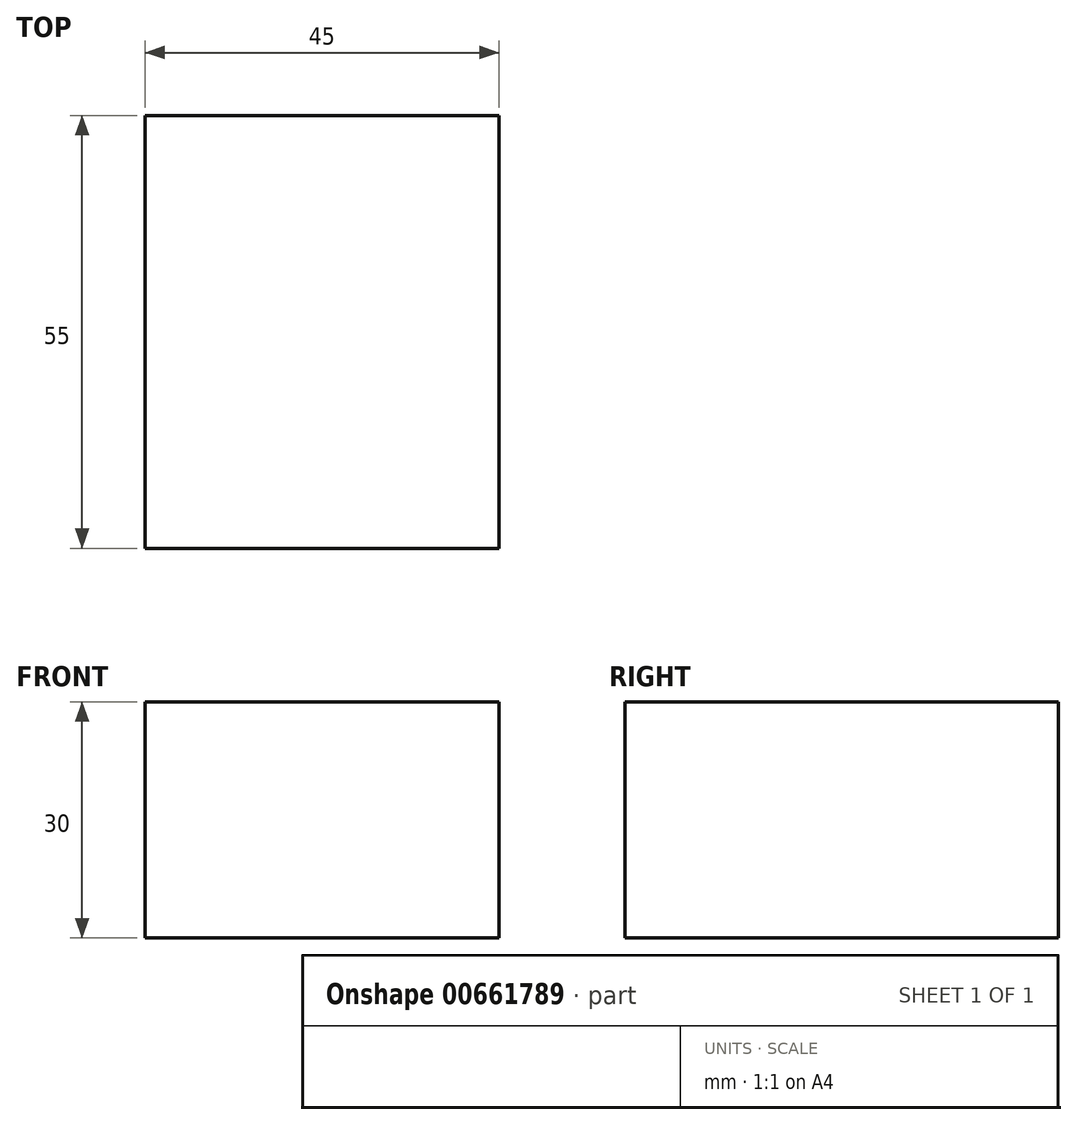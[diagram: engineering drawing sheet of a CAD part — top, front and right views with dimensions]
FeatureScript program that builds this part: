
annotation { "Feature Type Name" : "Feature", "Feature Type Description" : "" }
export const myFeature = defineFeature(function(context is Context, id is Id, definition is map)
    precondition{}
    {
        {
            var Q0;
            Q0=qCreatedBy(makeId("Top.planeOp"),FACE);
            var sketch = newSketch(context, id + "F0", { "sketchPlane" : qUnion([Q0])});
            skLineSegment(sketch, "E0.bottom", {"start": v(0, 0) * mm, "end": v(45, 0) * mm});
            skLineSegment(sketch, "E0.top", {"start": v(0, 55) * mm, "end": v(45, 55) * mm});
            skLineSegment(sketch, "E0.left", {"start": v(0, 0) * mm, "end": v(0, 55) * mm});
            skLineSegment(sketch, "E0.right", {"start": v(45, 0) * mm, "end": v(45, 55) * mm});
            skLineSegment(sketch, "E1.bottom", {"start": v(26.08, -4.61) * mm, "end": v(59.08, -4.61) * mm});
            skLineSegment(sketch, "E1.top", {"start": v(26.08, -29.61) * mm, "end": v(59.08, -29.61) * mm});
            skLineSegment(sketch, "E1.left", {"start": v(26.08, -4.61) * mm, "end": v(26.08, -29.61) * mm});
            skLineSegment(sketch, "E1.right", {"start": v(59.08, -4.61) * mm, "end": v(59.08, -29.61) * mm});
            skSolve(sketch);
        }
        {
            var Q0;
            Q0=makeQuery(id+"F0.imprint","IMPRINT",FACE,{"disambiguationData":[TD([[makeQuery(id+"F0.imprint","IMPRINT",EDGE,{"derivedFrom":sQuery(id+"F0.wireOp",EDGE,"E0.bottom")}),1.0]])]});
            extrude(context, id + "F1", {"entities" : qUnion([Q0]), "depth" : 30 * mm, "offsetDistance" : 25 * mm});
        }
    });
